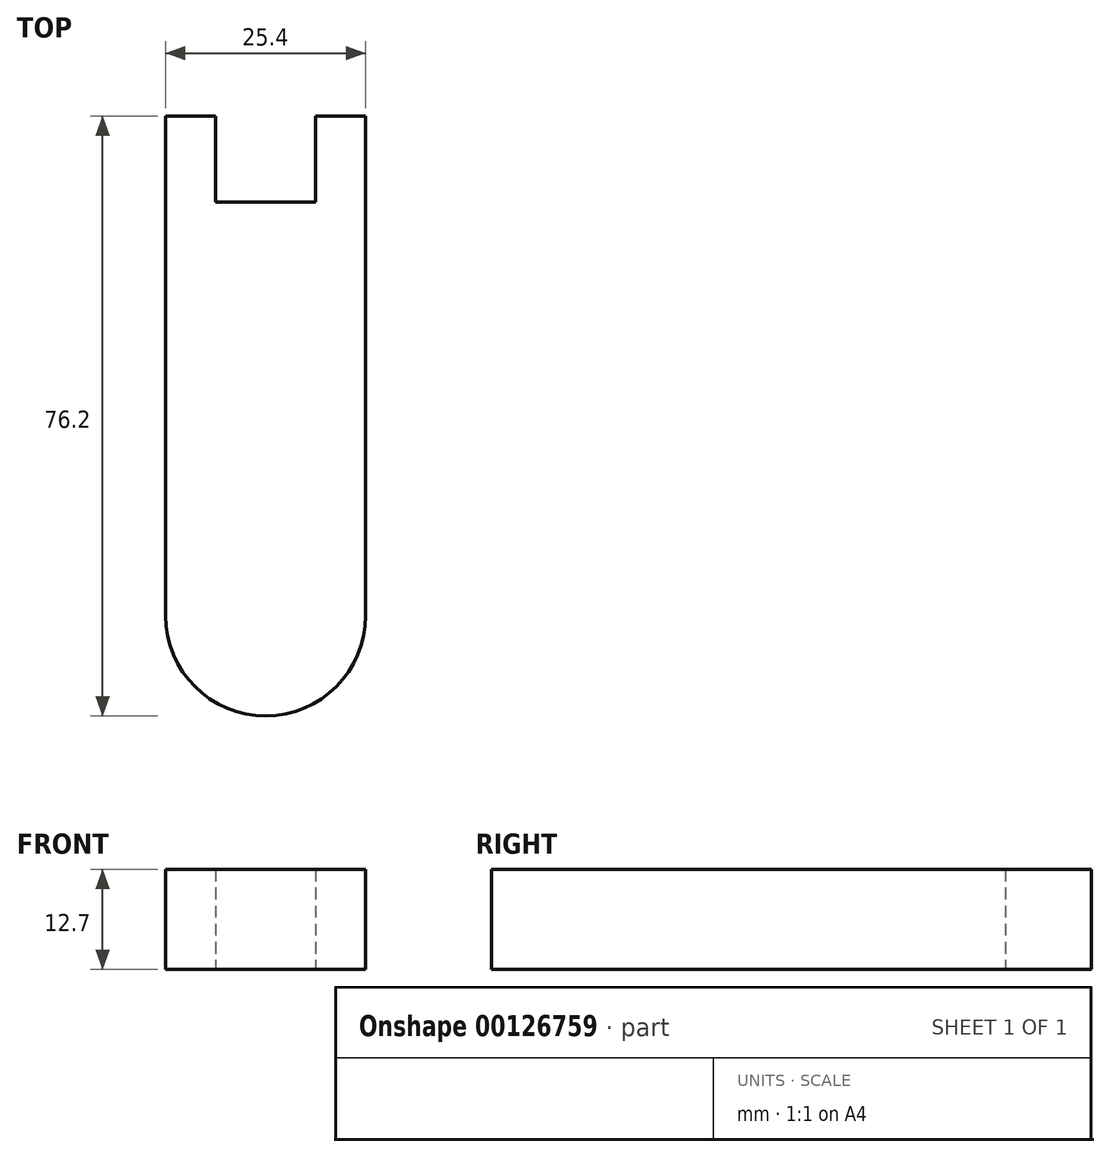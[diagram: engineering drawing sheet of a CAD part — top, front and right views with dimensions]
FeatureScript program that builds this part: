
annotation { "Feature Type Name" : "Feature", "Feature Type Description" : "" }
export const myFeature = defineFeature(function(context is Context, id is Id, definition is map)
    precondition{}
    {
        {
            var Q0;
            Q0=qCreatedBy(makeId("Top.planeOp"),FACE);
            var sketch = newSketch(context, id + "F0", { "sketchPlane" : qUnion([Q0])});
            skLineSegment(sketch, "E0", {"start": v(-10.7, 33.01) * mm, "end": v(14.7, 33.01) * mm});
            skLineSegment(sketch, "E1", {"start": v(14.7, 33.01) * mm, "end": v(14.7, -30.49) * mm});
            skLineSegment(sketch, "E2", {"start": v(14.7, -30.49) * mm, "end": v(-10.7, -30.49) * mm});
            skLineSegment(sketch, "E3", {"start": v(-10.7, 33.01) * mm, "end": v(-10.7, -30.49) * mm});
            skLineSegment(sketch, "E4", {"start": v(-4.36, 33.01) * mm, "end": v(-4.36, 22.1) * mm});
            skLineSegment(sketch, "E5", {"start": v(-4.36, 22.1) * mm, "end": v(8.34, 22.1) * mm});
            skLineSegment(sketch, "E6", {"start": v(8.34, 22.1) * mm, "end": v(8.34, 33.01) * mm});
            skArc(sketch, "E7", {"start": v(-10.7, -30.49) * mm, "mid": v(2, -43.19) * mm, "end": v(14.7, -30.49) * mm});
            skSolve(sketch);
        }
        {
            var Q0;
            {var subQ0=sQuery(id+"F0.wireOp",EDGE,"E1");Q0=makeQuery(id+"F0.imprint","IMPRINT",FACE,{"disambiguationData":[TD([[makeQuery(id+"F0.imprint","IMPRINT",EDGE,{"derivedFrom":subQ0}),-1.0]])]});}
            var Q1;
            Q1=makeQuery(id+"F0.imprint","IMPRINT",FACE,{"disambiguationData":[TD([[makeQuery(id+"F0.imprint","IMPRINT",EDGE,{"derivedFrom":sQuery(id+"F0.wireOp",EDGE,"E2")}),1.0]])]});
            extrude(context, id + "F1", {"entities" : qUnion([Q0, Q1]), "depth" : 12.7 * mm});
        }
    });
